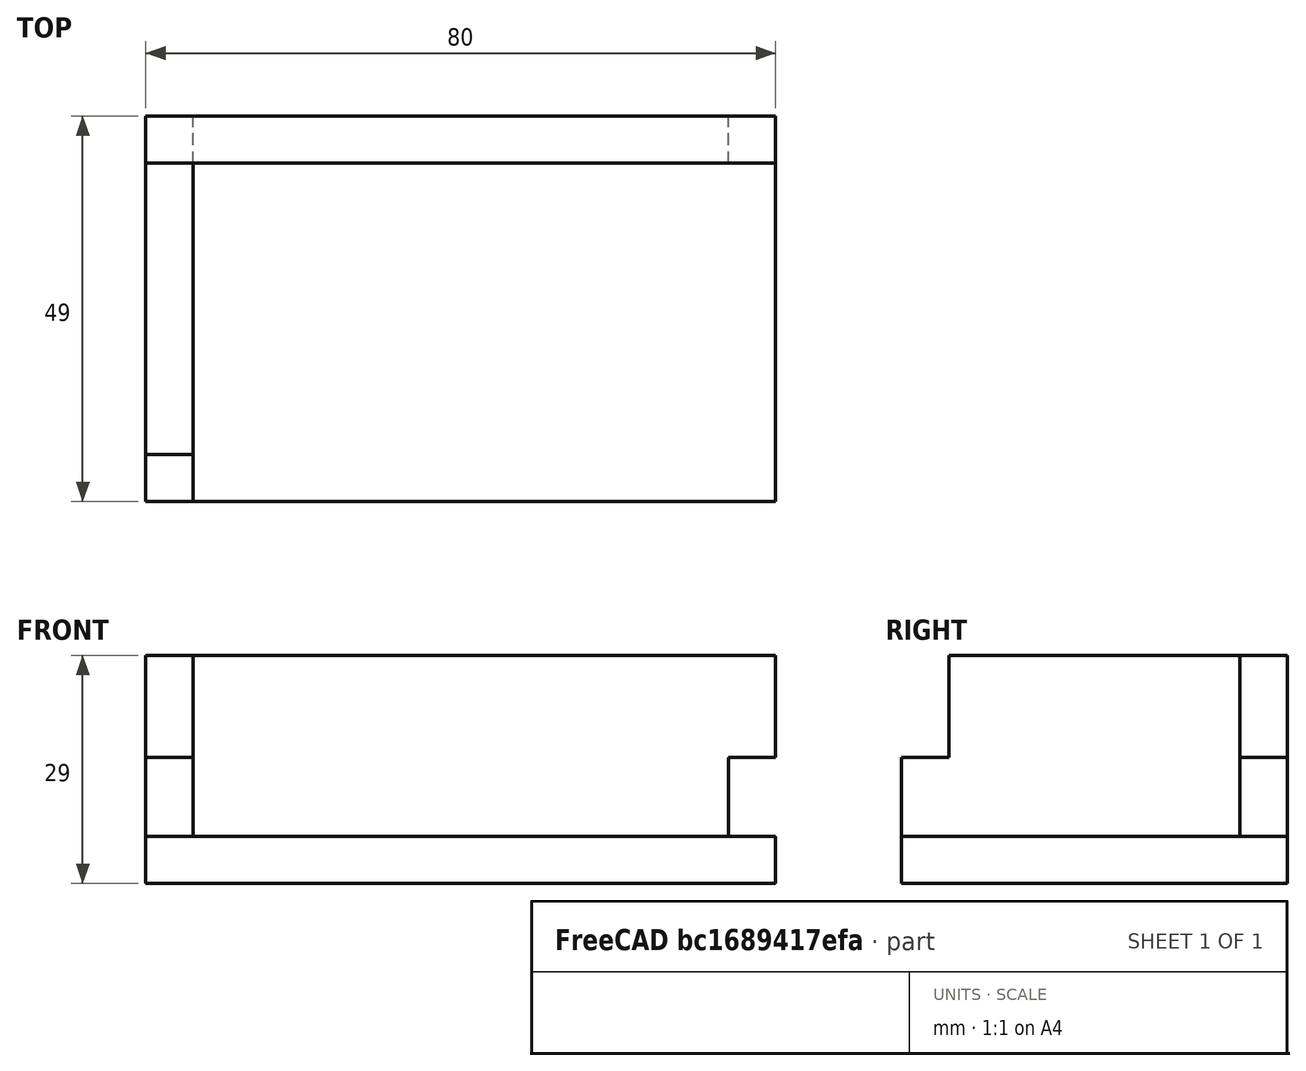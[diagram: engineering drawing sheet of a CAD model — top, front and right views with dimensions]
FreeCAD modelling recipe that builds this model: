
FCSTD DOCUMENT  (FreeCAD 0.18R16146 (Git))
Label: brass birmingham - beer tray
License: All rights reserved
LicenseURL: http://en.wikipedia.org/wiki/All_rights_reserved
objects: TechDraw::DrawViewPart×7, Sketcher::SketchObject×5, PartDesign::Body×5, PartDesign::Pad×3, Spreadsheet::Sheet×2, PartDesign::Pocket×2, PartDesign::FeatureBase×2, App::DocumentObjectGroup×2, TechDraw::DrawSVGTemplate×2, TechDraw::DrawViewDimension×2, TechDraw::DrawPage×2
note: 22 computed .brp shape members not serialized (recipe doc carries the construction recipe); baked Part::Feature solids carry a one-line shape summary decoded from their .brp

FEATURE [Spreadsheet::Sheet] Spreadsheet  label="my_variables"
  cells = A1=foam_width; B1(foam_width)==6mm; A3=outer height (minus base); B3(height_adjusted)==29mm - B1; A4=outer long width; B4(width_long)==80mm; A5=outer short width; B5(width_short)==50mm
FEATURE [Sketcher::SketchObject] Sketch
  MapMode = 5
  Support = -> [XY_Plane]
  expr: Constraints[9] = my_variables001.width_short
  expr: Constraints[10] = my_variables001.width_long
  sketch-geometry (4):
    g0: LineSegment StartX=-40 StartY=49 StartZ=0 EndX=40 EndY=49 EndZ=0
    g1: LineSegment StartX=40 StartY=49 StartZ=0 EndX=40 EndY=0 EndZ=0
    g2: LineSegment StartX=40 StartY=0 StartZ=0 EndX=-40 EndY=0 EndZ=0
    g3: LineSegment StartX=-40 StartY=0 StartZ=0 EndX=-40 EndY=49 EndZ=0
  constraints (11):
    c: Coincident(g0,g1)
    c: Coincident(g1,g2)
    c: Coincident(g2,g3)
    c: Coincident(g3,g0)
    c: Horizontal(g0)
    c: Horizontal(g2)
    c: Vertical(g1)
    c: Vertical(g3)
    c: Symmetric(g2,g2,g-1)
    c: Distance(g3) = 49
    c: Distance(g2) = 80
FEATURE [PartDesign::Pad] Pad
  Length = 6
  Length2 = 100
  Profile = -> Sketch
  Type = 0
  expr: Length = my_variables.foam_width
FEATURE [PartDesign::Body] Body  label="base"
  Group = -> [Sketch,Pad]
  Origin = -> Origin
  Tip = -> Pad
FEATURE [Sketcher::SketchObject] Sketch001
  MapMode = 5
  Placement = pos=(0,0,0) rot=(1,0,0;1.5708rad)
  Support = -> [XZ_Plane001]
  expr: Constraints[10] = my_variables001.width_long
  expr: Constraints[9] = my_variables001.height_adjusted
  sketch-geometry (4):
    g0: LineSegment StartX=-40 StartY=23 StartZ=0 EndX=40 EndY=23 EndZ=0
    g1: LineSegment StartX=40 StartY=23 StartZ=0 EndX=40 EndY=0 EndZ=0
    g2: LineSegment StartX=40 StartY=0 StartZ=0 EndX=-40 EndY=0 EndZ=0
    g3: LineSegment StartX=-40 StartY=0 StartZ=0 EndX=-40 EndY=23 EndZ=0
  constraints (11):
    c: Coincident(g0,g1)
    c: Coincident(g1,g2)
    c: Coincident(g2,g3)
    c: Coincident(g3,g0)
    c: Horizontal(g0)
    c: Horizontal(g2)
    c: Vertical(g1)
    c: Vertical(g3)
    c: Symmetric(g2,g2,g-1)
    c: Distance(g3) = 23
    c: Distance(g0) = 80
FEATURE [PartDesign::Pad] Pad001
  Length = 6
  Length2 = 100
  Placement = pos=(0,0,0) rot=(1,0,0;1.5708rad)
  Profile = -> Sketch001
  Type = 0
  expr: Length = my_variables.foam_width
FEATURE [Sketcher::SketchObject] Sketch002
  MapMode = 5
  Placement = pos=(0,-6,-1.3e-15) rot=(1,0,0;1.5708rad)
  Support = -> [Pad001]
  expr: Constraints[30] = my_variables.foam_width
  expr: Constraints[29] = my_variables.foam_width
  expr: Constraints[10] = Sketch001.Constraints[10]
  expr: Constraints[9] = Sketch001.Constraints[9]
  sketch-geometry (12):
    g0: LineSegment [constr] StartX=-40 StartY=23 StartZ=0 EndX=40 EndY=23 EndZ=0
    g1: LineSegment [constr] StartX=40 StartY=23 StartZ=0 EndX=40 EndY=0 EndZ=0
    g2: LineSegment [constr] StartX=40 StartY=0 StartZ=0 EndX=-40 EndY=0 EndZ=0
    g3: LineSegment [constr] StartX=-40 StartY=0 StartZ=0 EndX=-40 EndY=23 EndZ=0
    g4: LineSegment StartX=-40 StartY=10 StartZ=0 EndX=-34 EndY=10 EndZ=0
    g5: LineSegment StartX=-34 StartY=10 StartZ=0 EndX=-34 EndY=0 EndZ=0
    g6: LineSegment StartX=-34 StartY=0 StartZ=0 EndX=-40 EndY=0 EndZ=0
    g7: LineSegment StartX=-40 StartY=0 StartZ=0 EndX=-40 EndY=10 EndZ=0
    g8: LineSegment StartX=34 StartY=10 StartZ=0 EndX=40 EndY=10 EndZ=0
    g9: LineSegment StartX=40 StartY=10 StartZ=0 EndX=40 EndY=0 EndZ=0
    g10: LineSegment StartX=40 StartY=0 StartZ=0 EndX=34 EndY=0 EndZ=0
    g11: LineSegment StartX=34 StartY=0 StartZ=0 EndX=34 EndY=10 EndZ=0
  constraints (33):
    c: Coincident(g0,g1)
    c: Coincident(g1,g2)
    c: Coincident(g2,g3)
    c: Coincident(g3,g0)
    c: Horizontal(g0)
    c: Horizontal(g2)
    c: Vertical(g1)
    c: Vertical(g3)
    c: Symmetric(g2,g2,g-1)
    c: Distance(g3) = 23
    c: Distance(g0) = 80
    c: Coincident(g4,g5)
    c: Coincident(g5,g6)
    c: Coincident(g6,g7)
    c: Coincident(g7,g4)
    c: Horizontal(g4)
    c: Horizontal(g6)
    c: Vertical(g5)
    c: Vertical(g7)
    c: Coincident(g8,g9)
    c: Coincident(g9,g10)
    c: Coincident(g10,g11)
    c: Coincident(g11,g8)
    c: Horizontal(g8)
    c: Horizontal(g10)
    c: Vertical(g9)
    c: Vertical(g11)
    c: Coincident(g6,g2)
    c: Coincident(g9,g1)
    c: Distance(g4) = 6
    c: Distance(g8) = 6
    c: Distance(g5) = 10
    c: Distance(g11) = 10
FEATURE [PartDesign::Pocket] Pocket
  BaseFeature = -> Pad001
  Length = 5
  Length2 = 100
  Placement = pos=(0,0,0) rot=(1,0,0;1.5708rad)
  Profile = -> Sketch002
  Type = 1
FEATURE [PartDesign::Body] Body001  label="side long"
  Group = -> [Sketch001,Pad001,Sketch002,Pocket]
  Origin = -> Origin001
  Placement = pos=(7e-15,6,6) rot=(0,0,1;0rad)
  Tip = -> Pocket
FEATURE [PartDesign::FeatureBase] Clone
  BaseFeature = -> Body001
  Placement = pos=(7e-15,6,6) rot=(0,0,1;0rad)
FEATURE [PartDesign::Body] Body002  label="side long - clone"
  BaseFeature = -> Body001
  Group = -> [Clone]
  Origin = -> Origin002
  Placement = pos=(0,43,-2e-14) rot=(0,0,1;0rad)
  Tip = -> Clone
FEATURE [Sketcher::SketchObject] Sketch003
  MapMode = 5
  Placement = pos=(0,0,0) rot=(0.57735,0.57735,0.57735;2.0944rad)
  Support = -> [YZ_Plane003]
  expr: Constraints[10] = my_variables001.width_short
  expr: Constraints[9] = my_variables001.height_adjusted
  sketch-geometry (4):
    g0: LineSegment StartX=-24.5 StartY=23 StartZ=0 EndX=24.5 EndY=23 EndZ=0
    g1: LineSegment StartX=24.5 StartY=23 StartZ=0 EndX=24.5 EndY=0 EndZ=0
    g2: LineSegment StartX=24.5 StartY=0 StartZ=0 EndX=-24.5 EndY=0 EndZ=0
    g3: LineSegment StartX=-24.5 StartY=0 StartZ=0 EndX=-24.5 EndY=23 EndZ=0
  constraints (11):
    c: Coincident(g0,g1)
    c: Coincident(g1,g2)
    c: Coincident(g2,g3)
    c: Coincident(g3,g0)
    c: Horizontal(g0)
    c: Horizontal(g2)
    c: Vertical(g1)
    c: Vertical(g3)
    c: Symmetric(g2,g2,g-1)
    c: Distance(g3) = 23
    c: Distance(g0) = 49
FEATURE [PartDesign::Pad] Pad002
  Length = 6
  Length2 = 100
  Placement = pos=(0,0,0) rot=(0.57735,0.57735,0.57735;2.0944rad)
  Profile = -> Sketch003
  Type = 0
  expr: Length = my_variables.foam_width
FEATURE [Sketcher::SketchObject] Sketch004
  MapMode = 5
  Placement = pos=(6,-2.7e-15,2e-15) rot=(0.57735,0.57735,0.57735;2.0944rad)
  Support = -> [Pad002]
  expr: Constraints[30] = my_variables.foam_width
  expr: Constraints[29] = my_variables.foam_width
  expr: Constraints[10] = Sketch003.Constraints[10]
  expr: Constraints[9] = Sketch003.Constraints[9]
  sketch-geometry (12):
    g0: LineSegment [constr] StartX=-24.5 StartY=23 StartZ=0 EndX=24.5 EndY=23 EndZ=0
    g1: LineSegment [constr] StartX=24.5 StartY=23 StartZ=0 EndX=24.5 EndY=0 EndZ=0
    g2: LineSegment [constr] StartX=24.5 StartY=0 StartZ=0 EndX=-24.5 EndY=0 EndZ=0
    g3: LineSegment [constr] StartX=-24.5 StartY=0 StartZ=0 EndX=-24.5 EndY=23 EndZ=0
    g4: LineSegment StartX=-18.5 StartY=10 StartZ=0 EndX=-24.5 EndY=10 EndZ=0
    g5: LineSegment StartX=-24.5 StartY=10 StartZ=0 EndX=-24.5 EndY=23 EndZ=0
    g6: LineSegment StartX=-24.5 StartY=23 StartZ=0 EndX=-18.5 EndY=23 EndZ=0
    g7: LineSegment StartX=-18.5 StartY=23 StartZ=0 EndX=-18.5 EndY=10 EndZ=0
    g8: LineSegment StartX=18.5 StartY=10 StartZ=0 EndX=24.5 EndY=10 EndZ=0
    g9: LineSegment StartX=24.5 StartY=10 StartZ=0 EndX=24.5 EndY=23 EndZ=0
    g10: LineSegment StartX=24.5 StartY=23 StartZ=0 EndX=18.5 EndY=23 EndZ=0
    g11: LineSegment StartX=18.5 StartY=23 StartZ=0 EndX=18.5 EndY=10 EndZ=0
  constraints (33):
    c: Coincident(g0,g1)
    c: Coincident(g1,g2)
    c: Coincident(g2,g3)
    c: Coincident(g3,g0)
    c: Horizontal(g0)
    c: Horizontal(g2)
    c: Vertical(g1)
    c: Vertical(g3)
    c: Symmetric(g2,g2,g-1)
    c: Distance(g3) = 23
    c: Distance(g0) = 49
    c: Coincident(g4,g5)
    c: Coincident(g5,g6)
    c: Coincident(g6,g7)
    c: Coincident(g7,g4)
    c: Horizontal(g4)
    c: Horizontal(g6)
    c: Vertical(g5)
    c: Vertical(g7)
    c: Coincident(g8,g9)
    c: Coincident(g9,g10)
    c: Coincident(g10,g11)
    c: Coincident(g11,g8)
    c: Horizontal(g8)
    c: Horizontal(g10)
    c: Vertical(g9)
    c: Vertical(g11)
    c: Coincident(g9,g0)
    c: Coincident(g5,g0)
    c: Distance(g4) = 6
    c: Distance(g8) = 6
    c: Distance(g2,g4) = 10
    c: Distance(g1,g8) = 10
FEATURE [PartDesign::Pocket] Pocket001
  BaseFeature = -> Pad002
  Length = 5
  Length2 = 100
  Placement = pos=(0,0,0) rot=(0.57735,0.57735,0.57735;2.0944rad)
  Profile = -> Sketch004
  Type = 1
FEATURE [PartDesign::Body] Body003  label="side short"
  Group = -> [Sketch003,Pad002,Sketch004,Pocket001]
  Origin = -> Origin003
  Placement = pos=(34,24.5,6) rot=(0,0,1;0rad)
  Tip = -> Pocket001
FEATURE [App::DocumentObjectGroup] Group  label="parts"
  Group = -> [Body,Body001,Body003]
FEATURE [PartDesign::FeatureBase] Clone001
  BaseFeature = -> Body003
  Placement = pos=(34,25,6) rot=(0,0,1;0rad)
FEATURE [PartDesign::Body] Body004  label="side small - clone"
  BaseFeature = -> Body003
  Group = -> [Clone001]
  Origin = -> Origin004
  Placement = pos=(-74,-0.5,-5e-15) rot=(0,0,1;0rad)
  Tip = -> Clone001
FEATURE [App::DocumentObjectGroup] Group001  label="clones"
  Group = -> [Body002,Body004]
FEATURE [TechDraw::DrawSVGTemplate] Template
  Height = 210
  Orientation = 1
  Width = 297
FEATURE [TechDraw::DrawViewPart] View002
  CoarseView = false
  Direction = (0,0,1)
  Focus = 100
  HardHidden = false
  IsoCount = 0
  IsoHidden = false
  IsoVisible = false
  LockPosition = false
  Perspective = false
  Rotation = 0
  ScaleType = 0
  SeamHidden = false
  SeamVisible = false
  SmoothHidden = false
  SmoothVisible = false
  Source = -> [Body]
  X = 62.9845
  Y = 172.655
FEATURE [TechDraw::DrawViewDimension] Dimension
  Arbitrary = false
  FormatSpec = %.2f
  LockPosition = false
  MeasureType = 1
  OverTolerance = 0
  References2D = -> [View002]
  Rotation = 0
  ScaleType = 0
  Type = 0
  UnderTolerance = 0
  X = -58.2835
  Y = 2.70619
FEATURE [TechDraw::DrawViewDimension] Dimension001
  Arbitrary = false
  FormatSpec = %.2f
  LockPosition = false
  MeasureType = 1
  OverTolerance = 0
  References2D = -> [View002]
  Rotation = 0
  ScaleType = 0
  Type = 0
  UnderTolerance = 0
  X = -1.35309
  Y = -38.1598
FEATURE [TechDraw::DrawViewPart] View003
  CoarseView = false
  Direction = (0,-1,0)
  Focus = 100
  HardHidden = false
  IsoCount = 0
  IsoHidden = false
  IsoVisible = false
  LockPosition = false
  Perspective = false
  Rotation = 0
  ScaleType = 0
  SeamHidden = false
  SeamVisible = false
  SmoothHidden = false
  SmoothVisible = false
  Source = -> [Body001]
  X = 63.2552
  Y = 99.0464
FEATURE [Spreadsheet::Sheet] Spreadsheet001  label="my_variables001"
  cells = A1=foam_width; B1(foam_width)==6mm; A3=outer height (minus base); B3(height_adjusted)==29mm - B1; A4=outer long width; B4(width_long)==80mm; A5=outer short width; B5(width_short)==49mm
FEATURE [TechDraw::DrawViewPart] View004
  CoarseView = false
  Direction = (0,-1,0)
  Focus = 100
  HardHidden = false
  IsoCount = 0
  IsoHidden = false
  IsoVisible = false
  LockPosition = false
  Perspective = false
  Rotation = 0
  ScaleType = 0
  SeamHidden = false
  SeamVisible = false
  SmoothHidden = false
  SmoothVisible = false
  Source = -> [Body001]
  X = 64.3376
  Y = 47.8995
FEATURE [TechDraw::DrawViewPart] View005
  CoarseView = false
  Direction = (1,0,0)
  Focus = 100
  HardHidden = false
  IsoCount = 0
  IsoHidden = false
  IsoVisible = false
  LockPosition = false
  Perspective = false
  Rotation = 0
  ScaleType = 0
  SeamHidden = false
  SeamVisible = false
  SmoothHidden = false
  SmoothVisible = false
  Source = -> [Body003]
  X = 188.822
  Y = 186.997
FEATURE [TechDraw::DrawViewPart] View006
  CoarseView = false
  Direction = (1,0,0)
  Focus = 100
  HardHidden = false
  IsoCount = 0
  IsoHidden = false
  IsoVisible = false
  LockPosition = false
  Perspective = false
  Rotation = 0
  ScaleType = 0
  SeamHidden = false
  SeamVisible = false
  SmoothHidden = false
  SmoothVisible = false
  Source = -> [Body003]
  X = 188.01
  Y = 141.534
FEATURE [TechDraw::DrawSVGTemplate] Template001
  Height = 210
  Orientation = 1
  Width = 297
FEATURE [TechDraw::DrawViewPart] View
  CoarseView = false
  Direction = (0.577,-0.577,0.577)
  Focus = 100
  HardHidden = false
  IsoCount = 0
  IsoHidden = false
  IsoVisible = false
  LockPosition = false
  Perspective = false
  Rotation = 0
  Scale = 1.5
  ScaleType = 0
  SeamHidden = false
  SeamVisible = false
  SmoothHidden = false
  SmoothVisible = false
  Source = -> [Body,Body004,Body003,Body002,Body001,Group001]
  X = 149.853
  Y = 105.812
FEATURE [TechDraw::DrawPage] Page001  label="iso view"
  KeepUpdated = true
  ProjectionType = 0
  Scale = 1.5
  Template = -> Template001
  Views = -> [View]
FEATURE [TechDraw::DrawViewPart] View007
  CoarseView = false
  Direction = (0,0,1)
  Focus = 100
  HardHidden = false
  IsoCount = 0
  IsoHidden = false
  IsoVisible = false
  LockPosition = false
  Perspective = false
  Rotation = 0
  ScaleType = 0
  SeamHidden = false
  SeamVisible = false
  SmoothHidden = false
  SmoothVisible = false
  Source = -> [Body,Body004,Body003,Body001,Body002,Group001]
  X = 183.951
  Y = 76.5851
FEATURE [TechDraw::DrawPage] Page  label="Parts"
  KeepUpdated = true
  ProjectionType = 0
  Template = -> Template
  Views = -> [View002,Dimension,Dimension001,View003,View004,View005,View006,View007]
